# Revit family: 3100.184 Down Pipe Junction SE80bf
name_source: partatom
category: Plumbing Fixtures
units: mm (PartAtom-declared; Revit-internal decimal feet)

## family parameters
Always vertical = Yes
Cut with Voids When Loaded = No
OmniClass Number = 23.13.41.39
Part Type = Normal
Room Calculation Point = No
Round Connector Dimension = Use Diameter
Shared = No
Work Plane-Based = No

## types (1)
- 3100.184 100x80
    CW Connection = No
    Default Elevation = 0 mm  [stored 0 ft]
    Description = Deck Drain Side Exit 100mm Inlet w 80mm Outlet Big Flange
    HW Connection = No
    Manufacturer = Aquanight Industries Ltd
    Model = 3100.184
    Not Vented = No
    URL = www.aquaknight.co.nz
    Vent Connection = No
    Vented = Yes
    Waste Connection = Yes

note: [stored X ft] marks values corroborated as IEEE doubles in the binary element streams (Revit-internal decimal feet)

## geometry (parser evidence)
native form markers: Sweep x2
no freeform markers — native parametric forms only
